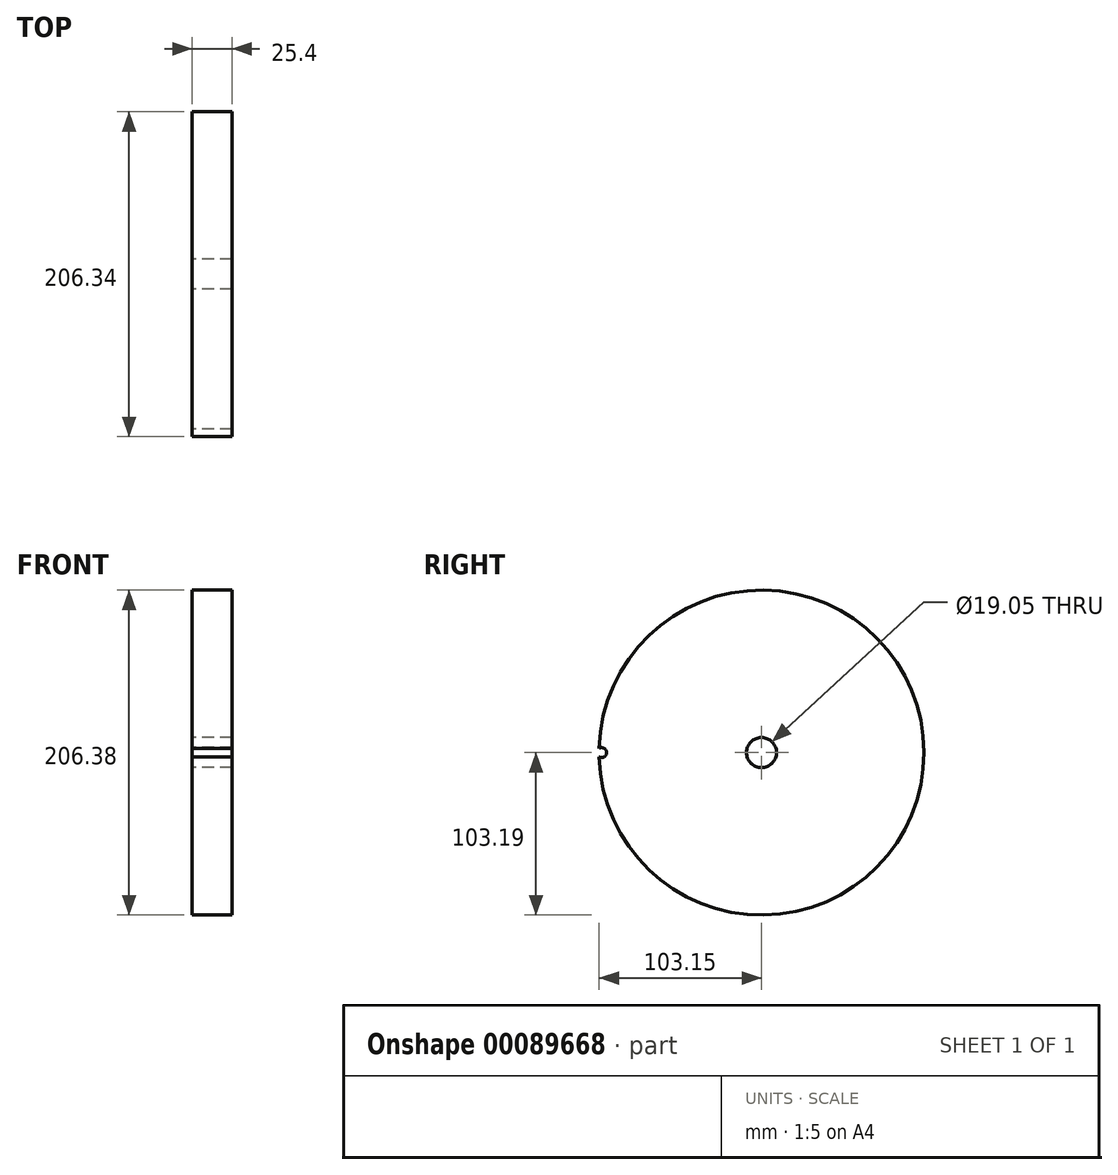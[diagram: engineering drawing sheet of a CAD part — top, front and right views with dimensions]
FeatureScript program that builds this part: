
annotation { "Feature Type Name" : "Feature", "Feature Type Description" : "" }
export const myFeature = defineFeature(function(context is Context, id is Id, definition is map)
    precondition{}
    {
        {
            var Q0;
            Q0=qCreatedBy(makeId("Right.planeOp"),FACE);
            var sketch = newSketch(context, id + "F0", { "sketchPlane" : qUnion([Q0])});
            skCircle(sketch, "E0", {"center": v(0, 0) * mm, "radius": 9.53 * mm});
            skCircle(sketch, "E1", {"center": v(-101.6, 0) * mm, "radius": 3.18 * mm});
            skCircle(sketch, "E2", {"center": v(0, 0) * mm, "radius": 103.19 * mm});
            skSolve(sketch);
        }
        {
            var Q0;
            Q0=makeQuery(id+"F0.imprint","IMPRINT",FACE,{"disambiguationData":[TD([[makeQuery(id+"F0.imprint","IMPRINT",EDGE,{"derivedFrom":sQuery(id+"F0.wireOp",EDGE,"E0")}),-1.0]])]});
            extrude(context, id + "F1", {"entities" : qUnion([Q0]), "endBound" : BoundingType.SYMMETRIC, "depth" : 25.4 * mm});
        }
    });
